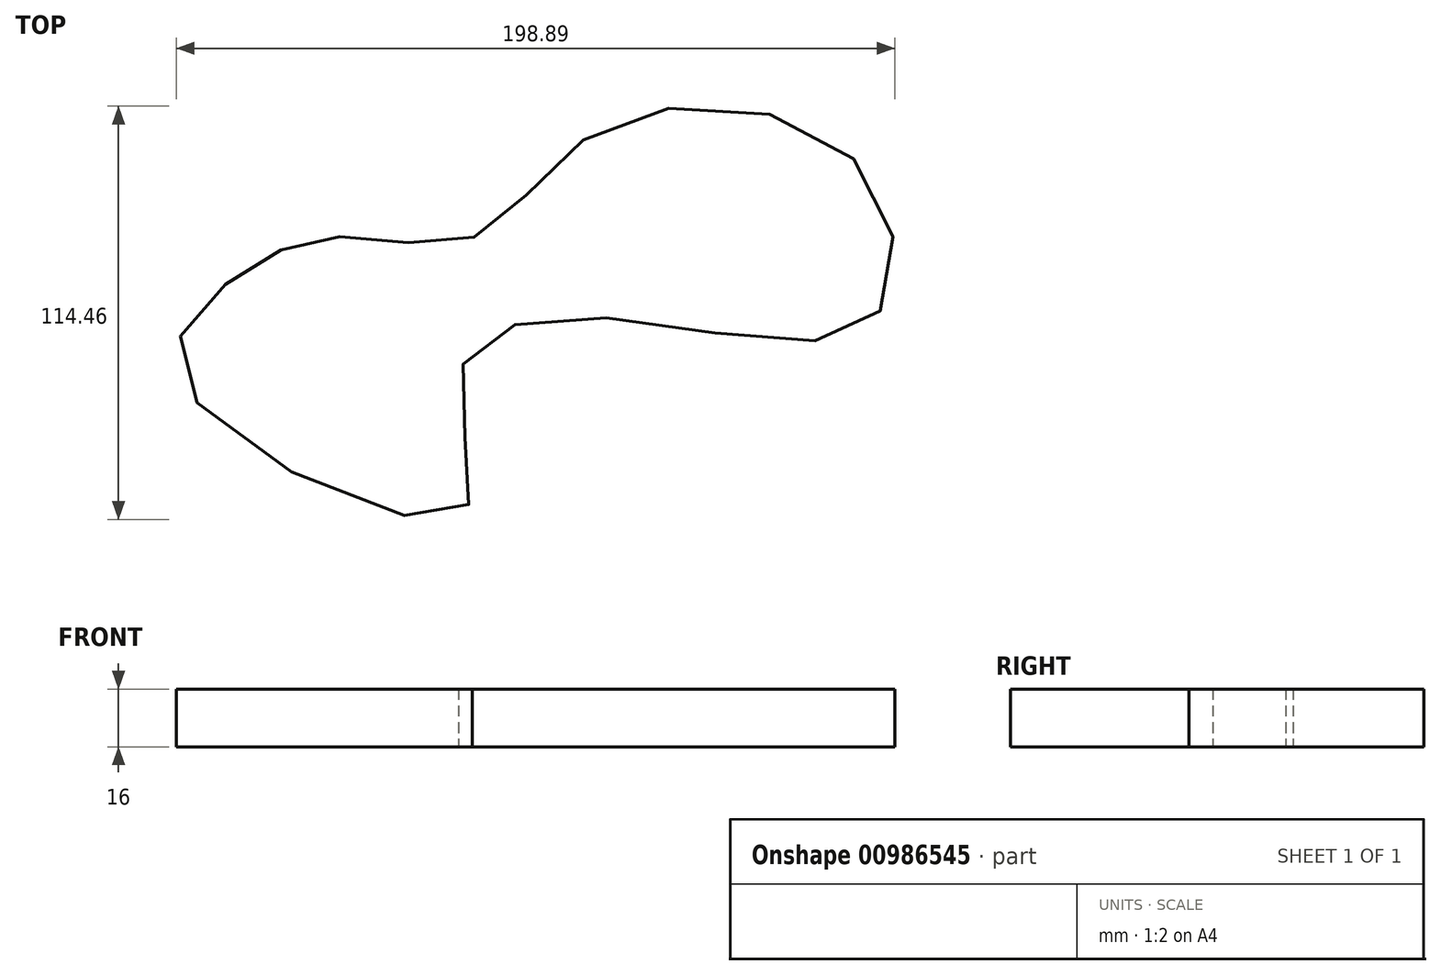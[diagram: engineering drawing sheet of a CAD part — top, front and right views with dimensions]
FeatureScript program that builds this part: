
annotation { "Feature Type Name" : "Feature", "Feature Type Description" : "" }
export const myFeature = defineFeature(function(context is Context, id is Id, definition is map)
    precondition{}
    {
        {
            var Q0;
            Q0=qCreatedBy(makeId("Top.planeOp"),FACE);
            var sketch = newSketch(context, id + "F0", { "sketchPlane" : qUnion([Q0])});
            skFitSpline(sketch, "E0", {"points": [v(0, 0) * mm, v(-29.06, -11.25) * mm, v(-43.38, -40.3) * mm, v(33.56, -76.73) * mm, v(33.15, -39.08) * mm, v(70.39, -22.3) * mm, v(146.5, -23.94) * mm, v(142.82, 21.08) * mm, v(72.84, 30.08) * mm, v(37.65, 0) * mm, v(0, 0) * mm]});
            skSolve(sketch);
        }
        {
            var Q0;
            Q0 = qSketchRegion(id + "F0", false);
            extrude(context, id + "F1", {"entities" : qUnion([Q0]), "depth" : 16 * mm});
        }
    });
